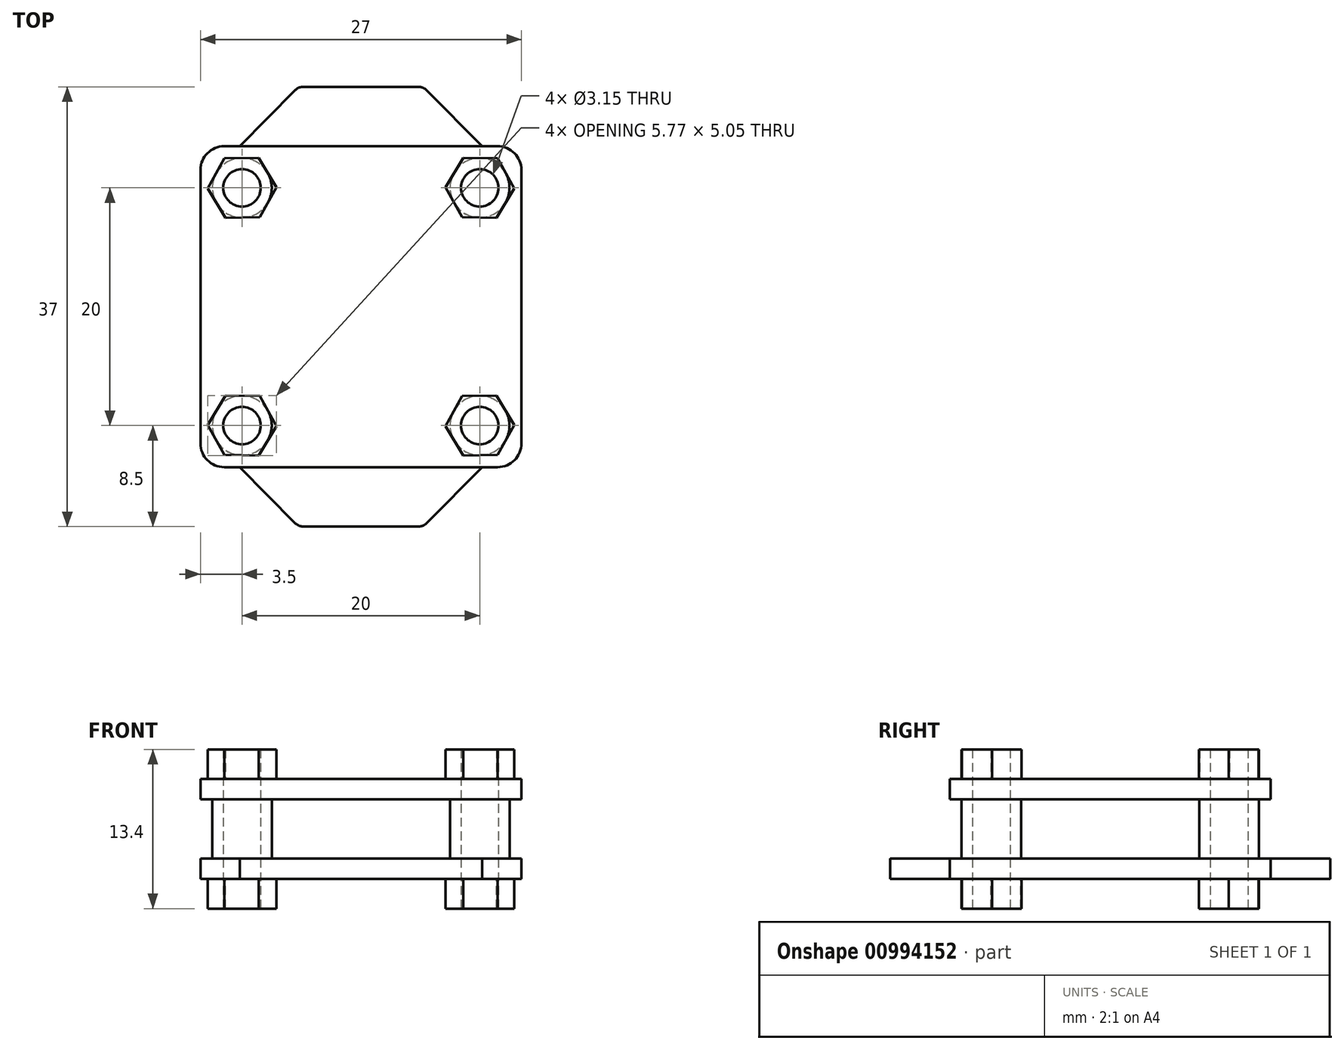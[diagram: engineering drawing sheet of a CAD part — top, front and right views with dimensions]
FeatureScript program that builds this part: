
annotation { "Feature Type Name" : "Feature", "Feature Type Description" : "" }
export const myFeature = defineFeature(function(context is Context, id is Id, definition is map)
    precondition{}
    {
        {
            assignVariable(context, id + "F0", {"name" : "BoardThickness", "anyValue" : 1.7 * mm});
        }
        {
            var Q0;
            Q0=qCreatedBy(makeId("Top.planeOp"),FACE);
            var sketch = newSketch(context, id + "F1", { "sketchPlane" : qUnion([Q0])});
            skCircle(sketch, "E0", {"center": v(-10, 10) * mm, "radius": 1.57 * mm});
            skCircle(sketch, "E1", {"center": v(10, 10) * mm, "radius": 1.57 * mm});
            skCircle(sketch, "E2", {"center": v(10, -10) * mm, "radius": 1.57 * mm});
            skCircle(sketch, "E3", {"center": v(-10, -10) * mm, "radius": 1.57 * mm});
            skLineSegment(sketch, "E4", {"start": v(10, 10) * mm, "end": v(-10, 10) * mm, "construction": true});
            skLineSegment(sketch, "E5", {"start": v(-10, 10) * mm, "end": v(-10, -10) * mm, "construction": true});
            skLineSegment(sketch, "E6", {"start": v(-10, -10) * mm, "end": v(10, -10) * mm, "construction": true});
            skLineSegment(sketch, "E7", {"start": v(10, -10) * mm, "end": v(10, 10) * mm, "construction": true});
            skPoint(sketch, "E8", {"position": v(0, 10) * mm});
            skPoint(sketch, "E9", {"position": v(-10, 0) * mm});
            skLineSegment(sketch, "E10.bottom", {"start": v(-11.5, 13.5) * mm, "end": v(11.5, 13.5) * mm});
            skLineSegment(sketch, "E10.top", {"start": v(-11.5, -13.5) * mm, "end": v(11.5, -13.5) * mm});
            skLineSegment(sketch, "E10.left", {"start": v(-13.5, 11.5) * mm, "end": v(-13.5, -11.5) * mm});
            skLineSegment(sketch, "E10.right", {"start": v(13.5, 11.5) * mm, "end": v(13.5, -11.5) * mm});
            skPoint(sketch, "E11", {"position": v(0, 13.5) * mm});
            skPoint(sketch, "E12", {"position": v(-13.5, 0) * mm});
            skPoint(sketch, "E13.visualSharp", {"position": v(-13.5, 13.5) * mm});
            skArc(sketch, "E13.filletArc", {"start": v(-11.5, 13.5) * mm, "mid": v(-12.91, 12.91) * mm, "end": v(-13.5, 11.5) * mm});
            skPoint(sketch, "E14.visualSharp", {"position": v(13.5, 13.5) * mm});
            skArc(sketch, "E14.filletArc", {"start": v(13.5, 11.5) * mm, "mid": v(12.91, 12.91) * mm, "end": v(11.5, 13.5) * mm});
            skPoint(sketch, "E15.visualSharp", {"position": v(13.5, -13.5) * mm});
            skArc(sketch, "E15.filletArc", {"start": v(11.5, -13.5) * mm, "mid": v(12.91, -12.91) * mm, "end": v(13.5, -11.5) * mm});
            skPoint(sketch, "E16.visualSharp", {"position": v(-13.5, -13.5) * mm});
            skArc(sketch, "E16.filletArc", {"start": v(-13.5, -11.5) * mm, "mid": v(-12.91, -12.91) * mm, "end": v(-11.5, -13.5) * mm});
            skLineSegment(sketch, "E17", {"start": v(-10.2, 13.5) * mm, "end": v(-5.54, 18.2) * mm});
            skLineSegment(sketch, "E18", {"start": v(-4.83, 18.5) * mm, "end": v(4.83, 18.5) * mm});
            skLineSegment(sketch, "E19", {"start": v(5.54, 18.2) * mm, "end": v(10.2, 13.5) * mm});
            skPoint(sketch, "E20", {"position": v(0, 18.5) * mm});
            skPoint(sketch, "E21.visualSharp", {"position": v(-5.25, 18.5) * mm});
            skArc(sketch, "E21.filletArc", {"start": v(-4.83, 18.5) * mm, "mid": v(-5.22, 18.42) * mm, "end": v(-5.54, 18.2) * mm});
            skPoint(sketch, "E22.visualSharp", {"position": v(5.25, 18.5) * mm});
            skArc(sketch, "E22.filletArc", {"start": v(5.54, 18.2) * mm, "mid": v(5.22, 18.42) * mm, "end": v(4.83, 18.5) * mm});
            skLineSegment(sketch, "E23.MirrorCS", {"start": v(5.54, -18.2) * mm, "end": v(10.2, -13.5) * mm});
            skArc(sketch, "E24.MirrorCS", {"start": v(5.54, -18.2) * mm, "mid": v(5.22, -18.42) * mm, "end": v(4.83, -18.5) * mm});
            skLineSegment(sketch, "E25.MirrorCS", {"start": v(-4.83, -18.5) * mm, "end": v(4.83, -18.5) * mm});
            skArc(sketch, "E26.MirrorCS", {"start": v(-4.83, -18.5) * mm, "mid": v(-5.22, -18.42) * mm, "end": v(-5.54, -18.2) * mm});
            skLineSegment(sketch, "E27.MirrorCS", {"start": v(-10.2, -13.5) * mm, "end": v(-5.54, -18.2) * mm});
            skSolve(sketch);
        }
        {
            var Q0;
            Q0 = qSketchRegion(id + "F1", true);
            extrude(context, id + "F2", {"entities" : qUnion([Q0]), "depth" : getVariable(context, 'BoardThickness'), "offsetDistance" : 25 * mm});
        }
        {
            var Q0;
            Q0=makeQuery(id+"F2.opExtrude","CAP_FACE",FACE,{"disambiguationData":[OSD([sQuery(id+"F1.wireOp",EDGE,"E0"),sQuery(id+"F1.wireOp",EDGE,"E1"),sQuery(id+"F1.wireOp",EDGE,"E2"),sQuery(id+"F1.wireOp",EDGE,"E3"),sQuery(id+"F1.wireOp",EDGE,"E10.bottom"),sQuery(id+"F1.wireOp",EDGE,"E10.top"),sQuery(id+"F1.wireOp",EDGE,"E10.left"),sQuery(id+"F1.wireOp",EDGE,"E10.right"),sQuery(id+"F1.wireOp",EDGE,"E13.filletArc"),sQuery(id+"F1.wireOp",EDGE,"E14.filletArc"),sQuery(id+"F1.wireOp",EDGE,"E15.filletArc"),sQuery(id+"F1.wireOp",EDGE,"E16.filletArc")])],"isStart":true});
            var sketch = newSketch(context, id + "F3", { "sketchPlane" : qUnion([Q0])});
            skCircle(sketch, "E28.0", {"center": v(-10, -10) * mm, "radius": 1.57 * mm});
            skCircle(sketch, "E29.0", {"center": v(-10, 10) * mm, "radius": 1.57 * mm});
            skCircle(sketch, "E30.cCircle", {"center": v(-10, -10) * mm, "radius": 2.5 * mm, "construction": true});
            skLineSegment(sketch, "E30.0", {"start": v(-12.89, -9.95) * mm, "end": v(-11.4, -7.48) * mm});
            skLineSegment(sketch, "E30.1", {"start": v(-11.4, -7.48) * mm, "end": v(-8.52, -7.52) * mm});
            skLineSegment(sketch, "E30.2", {"start": v(-8.52, -7.52) * mm, "end": v(-7.11, -10.05) * mm});
            skLineSegment(sketch, "E30.3", {"start": v(-7.11, -10.05) * mm, "end": v(-8.6, -12.52) * mm});
            skLineSegment(sketch, "E30.4", {"start": v(-8.6, -12.52) * mm, "end": v(-11.48, -12.48) * mm});
            skLineSegment(sketch, "E30.5", {"start": v(-11.48, -12.48) * mm, "end": v(-12.89, -9.95) * mm});
            skPoint(sketch, "E30.0.midPoint", {"position": v(-12.14, -8.71) * mm});
            skLineSegment(sketch, "E31.MirrorCS", {"start": v(-11.4, 7.48) * mm, "end": v(-8.52, 7.52) * mm});
            skLineSegment(sketch, "E32.MirrorCS", {"start": v(-8.52, 7.52) * mm, "end": v(-7.11, 10.05) * mm});
            skLineSegment(sketch, "E33.MirrorCS", {"start": v(-12.89, 9.95) * mm, "end": v(-11.4, 7.48) * mm});
            skLineSegment(sketch, "E34.MirrorCS", {"start": v(-11.48, 12.48) * mm, "end": v(-12.89, 9.95) * mm});
            skLineSegment(sketch, "E35.MirrorCS", {"start": v(-8.6, 12.52) * mm, "end": v(-11.48, 12.48) * mm});
            skLineSegment(sketch, "E36.MirrorCS", {"start": v(-7.11, 10.05) * mm, "end": v(-8.6, 12.52) * mm});
            skLineSegment(sketch, "E37.MirrorCS", {"start": v(12.89, -9.95) * mm, "end": v(11.4, -7.48) * mm});
            skLineSegment(sketch, "E38.MirrorCS", {"start": v(7.11, 10.05) * mm, "end": v(8.6, 12.52) * mm});
            skLineSegment(sketch, "E39.MirrorCS", {"start": v(11.48, 12.48) * mm, "end": v(12.89, 9.95) * mm});
            skLineSegment(sketch, "E40.MirrorCS", {"start": v(8.6, -12.52) * mm, "end": v(11.48, -12.48) * mm});
            skCircle(sketch, "E41.MirrorC", {"center": v(10, -10) * mm, "radius": 1.57 * mm});
            skPoint(sketch, "E42.MirrorP", {"position": v(12.14, -8.71) * mm});
            skLineSegment(sketch, "E43.MirrorCS", {"start": v(11.48, -12.48) * mm, "end": v(12.89, -9.95) * mm});
            skLineSegment(sketch, "E44.MirrorCS", {"start": v(12.89, 9.95) * mm, "end": v(11.4, 7.48) * mm});
            skLineSegment(sketch, "E45.MirrorCS", {"start": v(8.52, -7.52) * mm, "end": v(7.11, -10.05) * mm});
            skLineSegment(sketch, "E46.MirrorCS", {"start": v(8.6, 12.52) * mm, "end": v(11.48, 12.48) * mm});
            skCircle(sketch, "E47.MirrorC", {"center": v(10, 10) * mm, "radius": 1.57 * mm});
            skLineSegment(sketch, "E48.MirrorCS", {"start": v(7.11, -10.05) * mm, "end": v(8.6, -12.52) * mm});
            skLineSegment(sketch, "E49.MirrorCS", {"start": v(11.4, 7.48) * mm, "end": v(8.52, 7.52) * mm});
            skLineSegment(sketch, "E50.MirrorCS", {"start": v(8.52, 7.52) * mm, "end": v(7.11, 10.05) * mm});
            skLineSegment(sketch, "E51.MirrorCS", {"start": v(11.4, -7.48) * mm, "end": v(8.52, -7.52) * mm});
            skSolve(sketch);
        }
        {
            var Q0;
            Q0 = qSketchRegion(id + "F3", true);
            extrude(context, id + "F4", {"entities" : qUnion([Q0]), "operationType" : NewBodyOperationType.ADD, "depth" : 2.5 * mm, "offsetDistance" : 25 * mm});
        }
        {
            var Q0;
            Q0=makeQuery(id+"F2.opExtrude","CAP_FACE",FACE,{"disambiguationData":[OSD([sQuery(id+"F1.wireOp",EDGE,"E0"),sQuery(id+"F1.wireOp",EDGE,"E1"),sQuery(id+"F1.wireOp",EDGE,"E2"),sQuery(id+"F1.wireOp",EDGE,"E3"),sQuery(id+"F1.wireOp",EDGE,"E10.bottom"),sQuery(id+"F1.wireOp",EDGE,"E10.top"),sQuery(id+"F1.wireOp",EDGE,"E10.left"),sQuery(id+"F1.wireOp",EDGE,"E10.right"),sQuery(id+"F1.wireOp",EDGE,"E13.filletArc"),sQuery(id+"F1.wireOp",EDGE,"E14.filletArc"),sQuery(id+"F1.wireOp",EDGE,"E15.filletArc"),sQuery(id+"F1.wireOp",EDGE,"E16.filletArc")])],"isStart":false});
            var sketch = newSketch(context, id + "F5", { "sketchPlane" : qUnion([Q0])});
            skCircle(sketch, "E52.0", {"center": v(-10, 10) * mm, "radius": 1.57 * mm});
            skCircle(sketch, "E53.0", {"center": v(-10, 10) * mm, "radius": 2.5 * mm});
            skCircle(sketch, "E54.0", {"center": v(10, 10) * mm, "radius": 2.5 * mm});
            skCircle(sketch, "E55.0", {"center": v(10, -10) * mm, "radius": 2.5 * mm});
            skCircle(sketch, "E56.0", {"center": v(-10, -10) * mm, "radius": 2.5 * mm});
            skCircle(sketch, "E57.0", {"center": v(-10, -10) * mm, "radius": 1.57 * mm});
            skCircle(sketch, "E58.MirrorC", {"center": v(10, -10) * mm, "radius": 1.57 * mm});
            skCircle(sketch, "E59.MirrorC", {"center": v(10, 10) * mm, "radius": 1.57 * mm});
            skSolve(sketch);
        }
        {
            var Q0;
            Q0 = qSketchRegion(id + "F5", true);
            extrude(context, id + "F6", {"entities" : qUnion([Q0]), "operationType" : NewBodyOperationType.ADD, "depth" : 5 * mm, "offsetDistance" : 25 * mm});
        }
        {
            var Q0;
            Q0=makeQuery(id+"F6.opExtrude","CAP_FACE",FACE,{"disambiguationData":[OSD([sQuery(id+"F5.wireOp",EDGE,"E52.0"),sQuery(id+"F5.wireOp",EDGE,"E53.0")])],"isStart":false});
            var sketch = newSketch(context, id + "F7", { "sketchPlane" : qUnion([Q0])});
            skCircle(sketch, "E60.0", {"center": v(-10, 10) * mm, "radius": 1.57 * mm});
            skCircle(sketch, "E61.0", {"center": v(-10, -10) * mm, "radius": 1.57 * mm});
            skArc(sketch, "E62.0", {"start": v(11.5, -13.5) * mm, "mid": v(12.91, -12.91) * mm, "end": v(13.5, -11.5) * mm});
            skLineSegment(sketch, "E63.0", {"start": v(13.5, 11.5) * mm, "end": v(13.5, -11.5) * mm});
            skLineSegment(sketch, "E64.0", {"start": v(-11.5, -13.5) * mm, "end": v(11.5, -13.5) * mm});
            skArc(sketch, "E65.0", {"start": v(-13.5, -11.5) * mm, "mid": v(-12.91, -12.91) * mm, "end": v(-11.5, -13.5) * mm});
            skLineSegment(sketch, "E66.0", {"start": v(-13.5, 11.5) * mm, "end": v(-13.5, -11.5) * mm});
            skArc(sketch, "E67.0", {"start": v(-11.5, 13.5) * mm, "mid": v(-12.91, 12.91) * mm, "end": v(-13.5, 11.5) * mm});
            skLineSegment(sketch, "E68.0", {"start": v(-11.5, 13.5) * mm, "end": v(11.5, 13.5) * mm});
            skArc(sketch, "E69.0", {"start": v(13.5, 11.5) * mm, "mid": v(12.91, 12.91) * mm, "end": v(11.5, 13.5) * mm});
            skCircle(sketch, "E70.MirrorC", {"center": v(10, -10) * mm, "radius": 1.57 * mm});
            skCircle(sketch, "E71.MirrorC", {"center": v(10, 10) * mm, "radius": 1.57 * mm});
            skSolve(sketch);
        }
        {
            var Q0;
            Q0 = qSketchRegion(id + "F7", true);
            extrude(context, id + "F8", {"entities" : qUnion([Q0]), "operationType" : NewBodyOperationType.ADD, "depth" : 1.7 * mm, "offsetDistance" : 25 * mm});
        }
        {
            var Q0;
            Q0=makeQuery(id+"F8.opExtrude","CAP_FACE",FACE,{"disambiguationData":[OSD([sQuery(id+"F7.wireOp",EDGE,"E60.0"),sQuery(id+"F7.wireOp",EDGE,"93cb280c-4da9-4ed3-a5ee-02a34284d231.0"),sQuery(id+"F7.wireOp",EDGE,"9e660ae7-4df2-483b-8971-ef7f0ba3bc97.0"),sQuery(id+"F7.wireOp",EDGE,"E61.0"),sQuery(id+"F7.wireOp",EDGE,"E62.0"),sQuery(id+"F7.wireOp",EDGE,"E63.0"),sQuery(id+"F7.wireOp",EDGE,"E64.0"),sQuery(id+"F7.wireOp",EDGE,"E65.0"),sQuery(id+"F7.wireOp",EDGE,"E66.0"),sQuery(id+"F7.wireOp",EDGE,"E67.0"),sQuery(id+"F7.wireOp",EDGE,"E68.0"),sQuery(id+"F7.wireOp",EDGE,"E69.0")])],"isStart":false});
            var sketch = newSketch(context, id + "F9", { "sketchPlane" : qUnion([Q0])});
            skLineSegment(sketch, "E72.0", {"start": v(-8.52, 7.52) * mm, "end": v(-7.11, 10.05) * mm});
            skLineSegment(sketch, "E72.1", {"start": v(11.4, -7.48) * mm, "end": v(8.52, -7.52) * mm});
            skLineSegment(sketch, "E72.2", {"start": v(12.89, -9.95) * mm, "end": v(11.4, -7.48) * mm});
            skLineSegment(sketch, "E72.3", {"start": v(11.48, 12.48) * mm, "end": v(12.89, 9.95) * mm});
            skLineSegment(sketch, "E72.4", {"start": v(8.52, 7.52) * mm, "end": v(7.11, 10.05) * mm});
            skLineSegment(sketch, "E72.5", {"start": v(7.11, -10.05) * mm, "end": v(8.6, -12.52) * mm});
            skLineSegment(sketch, "E72.7", {"start": v(-8.6, 12.52) * mm, "end": v(-11.48, 12.48) * mm});
            skLineSegment(sketch, "E72.8", {"start": v(-7.11, 10.05) * mm, "end": v(-8.6, 12.52) * mm});
            skCircle(sketch, "E72.9", {"center": v(-10, 10) * mm, "radius": 1.57 * mm});
            skLineSegment(sketch, "E72.10", {"start": v(8.6, -12.52) * mm, "end": v(11.48, -12.48) * mm});
            skLineSegment(sketch, "E72.11", {"start": v(7.11, 10.05) * mm, "end": v(8.6, 12.52) * mm});
            skCircle(sketch, "E72.12", {"center": v(-10, -10) * mm, "radius": 1.57 * mm});
            skLineSegment(sketch, "E72.13", {"start": v(-8.6, -12.52) * mm, "end": v(-11.48, -12.48) * mm});
            skCircle(sketch, "E72.14", {"center": v(10, 10) * mm, "radius": 1.57 * mm});
            skLineSegment(sketch, "E72.15", {"start": v(-12.89, -9.95) * mm, "end": v(-11.4, -7.48) * mm});
            skLineSegment(sketch, "E72.17", {"start": v(11.48, -12.48) * mm, "end": v(12.89, -9.95) * mm});
            skLineSegment(sketch, "E72.18", {"start": v(-12.89, 9.95) * mm, "end": v(-11.4, 7.48) * mm});
            skLineSegment(sketch, "E72.19", {"start": v(8.6, 12.52) * mm, "end": v(11.48, 12.48) * mm});
            skLineSegment(sketch, "E72.20", {"start": v(-8.52, -7.52) * mm, "end": v(-7.11, -10.05) * mm});
            skCircle(sketch, "E72.21", {"center": v(10, -10) * mm, "radius": 1.57 * mm});
            skLineSegment(sketch, "E72.22", {"start": v(12.89, 9.95) * mm, "end": v(11.4, 7.48) * mm});
            skLineSegment(sketch, "E72.23", {"start": v(-11.4, 7.48) * mm, "end": v(-8.52, 7.52) * mm});
            skLineSegment(sketch, "E72.24", {"start": v(8.52, -7.52) * mm, "end": v(7.11, -10.05) * mm});
            skLineSegment(sketch, "E72.25", {"start": v(-11.4, -7.48) * mm, "end": v(-8.52, -7.52) * mm});
            skLineSegment(sketch, "E72.26", {"start": v(-11.48, -12.48) * mm, "end": v(-12.89, -9.95) * mm});
            skLineSegment(sketch, "E72.27", {"start": v(11.4, 7.48) * mm, "end": v(8.52, 7.52) * mm});
            skLineSegment(sketch, "E72.28", {"start": v(-7.11, -10.05) * mm, "end": v(-8.6, -12.52) * mm});
            skLineSegment(sketch, "E72.29", {"start": v(-11.48, 12.48) * mm, "end": v(-12.89, 9.95) * mm});
            skSolve(sketch);
        }
        {
            var Q0;
            Q0 = qSketchRegion(id + "F9", true);
            extrude(context, id + "F10", {"entities" : qUnion([Q0]), "operationType" : NewBodyOperationType.ADD, "depth" : 2.5 * mm, "offsetDistance" : 25 * mm});
        }
    });
